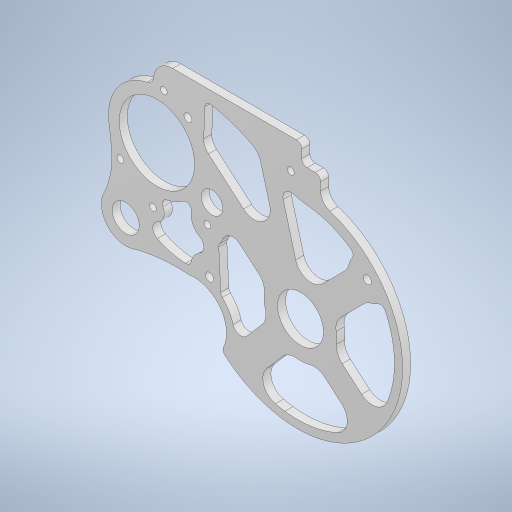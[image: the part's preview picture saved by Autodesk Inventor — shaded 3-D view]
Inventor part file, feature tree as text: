
AUTODESK INVENTOR PART (.ipt)
format: ipt  version: 2023.1 (Build 271208000, 208)  size: 573,952 bytes
history: native  units: mm
features: sketch x1, extrude x1, other x1, projected_geometry x1
ambient origin geometry x8: Origin, YZ Plane, XZ Plane, XY Plane, X Axis, Y Axis, Z Axis, Center Point
bodies: Solid3 (feature_tree)
feature tree (4):
  sketch  "Sketch9"  dims[d479=3.0mm d480=0.0mm d572=2.0mm d573=42.0mm d574=12.915436mm d575=20.594885mm d576=6.0mm d577=8.0mm d578=6.0mm d579=3.0mm d580=2.5mm d581=2.5mm d582=8.5mm d583=45.1mm d584=2.5mm d585=18.0mm d586=33.0mm d587=2.0mm d588=2.0mm d589=3.0mm d590=3.0mm d591=3.0mm d592=4.0mm d593=2.0mm d594=2.0mm d595=3.0mm d596=2.0mm d597=3.0mm d598=3.0mm d599=2.0mm d600=2.0mm d601=3.0mm d602=2.0mm d603=3.0mm d604=12.0mm d605=3.0mm d606=2.0mm d607=3.0mm d608=3.0mm d609=3.0mm d610=3.0mm d611=2.0mm d612=3.0mm d613=3.0mm d614=2.0mm d615=6.0mm d616=4.0mm d617=17.05mm d618=5.0mm d619=3.0mm d620=6.0mm d621=6.0mm d622=6.0mm d623=6.0mm d624=6.0mm d625=10.0mm d626=5.0mm d627=4.0mm d628=5.0mm d629=6.0mm d630=6.0mm d631=10.0mm d632=5.0mm d633=6.0mm d634=6.0mm d635=6.0mm d636=6.0mm d637=10.0mm d638=3.0mm d639=6.0mm d640=8.05mm d641=6.0mm d642=6.0mm d643=3.0mm d644=10.05mm d645=35.0mm d646=4.0mm d647=60.0mm d648=10.0mm d649=5.0mm d650=6.0mm d651=3.0mm d652=4.5mm d653=54.0mm d654=60.0deg d655=6.0mm d656=30.0mm d657=3.0mm d658=5.0mm d659=2.5mm d660=30.0mm d663=45.0deg d664=2.5mm d665=13.213299mm d666=6.606649mm d115=0.5mm d116=0.872665mm d117=0.5mm d118=0.872665mm d368=0.5mm d369=0.872665mm d370=0.5mm d371=0.872665mm]
  extrude  "Extrusion8"  TaperAngle=45.0deg  [1 undecoded]
  other  "sesaku"
  projected_geometry  "Projected Loop3"
note: 1 required parameter value undecoded (feature->parameter linkage not recoverable at this tier; creation-order binding heuristic only, values carry confidence <= 0.55)
